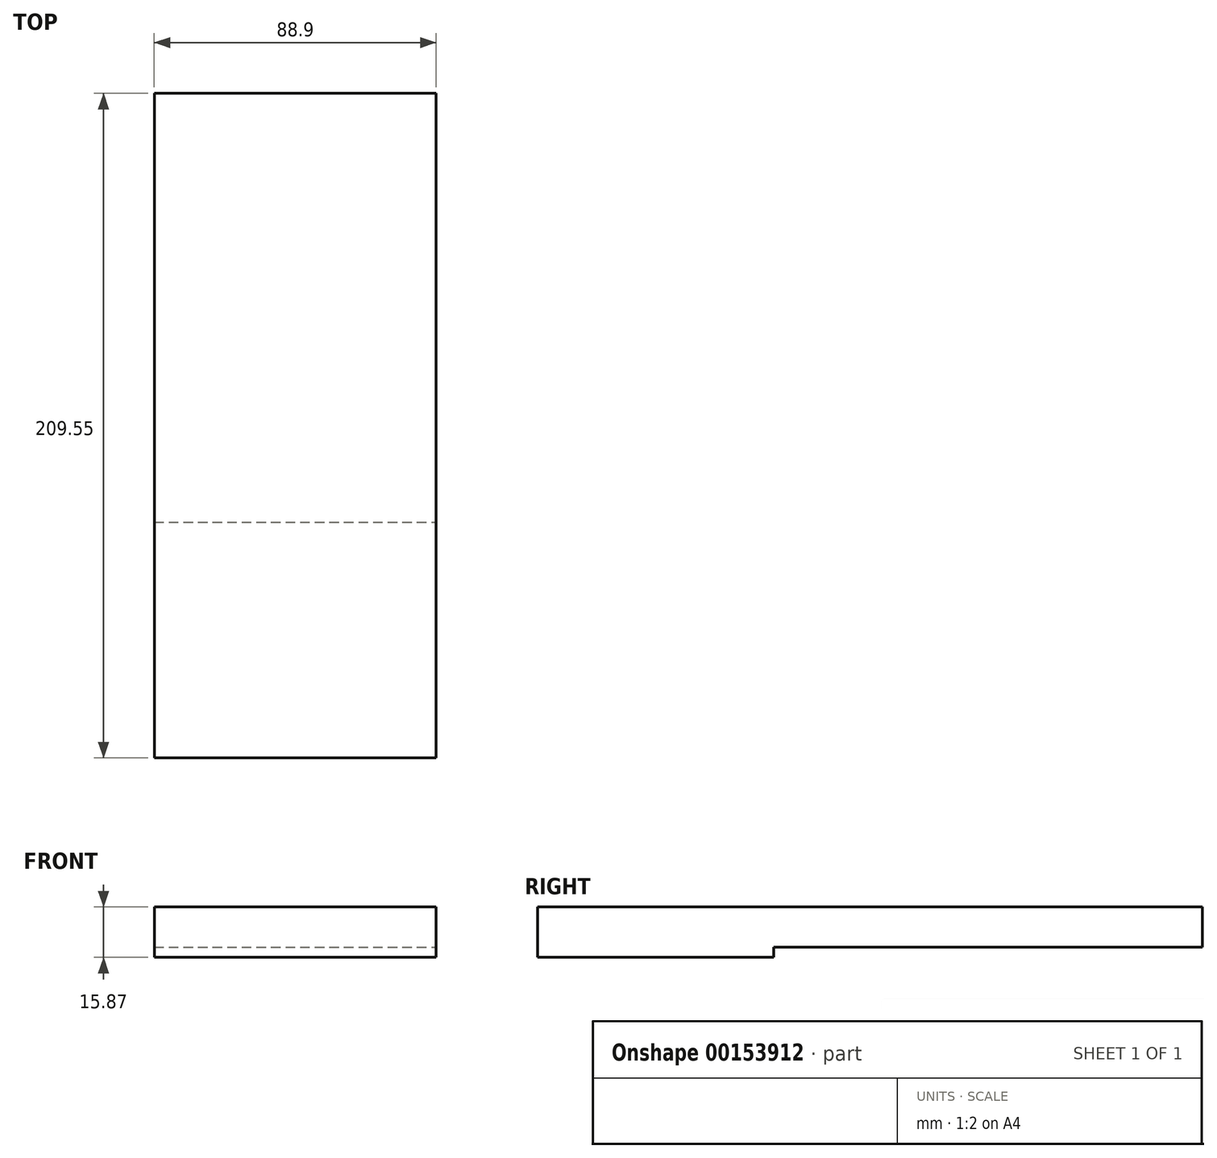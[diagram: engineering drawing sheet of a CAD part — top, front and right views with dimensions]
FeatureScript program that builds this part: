
annotation { "Feature Type Name" : "Feature", "Feature Type Description" : "" }
export const myFeature = defineFeature(function(context is Context, id is Id, definition is map)
    precondition{}
    {
        {
            var Q0;
            Q0=qCreatedBy(makeId("Front.planeOp"),FACE);
            var sketch = newSketch(context, id + "F0", { "sketchPlane" : qUnion([Q0])});
            skLineSegment(sketch, "E0.bottom", {"start": v(-33.87, 12.7) * mm, "end": v(55.03, 12.7) * mm});
            skLineSegment(sketch, "E0.top", {"start": v(-33.87, 0) * mm, "end": v(55.03, 0) * mm});
            skLineSegment(sketch, "E0.left", {"start": v(-33.87, 12.7) * mm, "end": v(-33.87, 0) * mm});
            skLineSegment(sketch, "E0.right", {"start": v(55.03, 12.7) * mm, "end": v(55.03, 0) * mm});
            skSolve(sketch);
        }
        {
            var Q0;
            Q0 = qSketchRegion(id + "F0", true);
            extrude(context, id + "F1", {"entities" : qUnion([Q0]), "depth" : 209.55 * mm});
        }
        {
            var Q0;
            Q0=makeQuery(id+"F1.opExtrude","SWEPT_FACE",FACE,{"disambiguationData":[OSD([sQuery(id+"F0.wireOp",EDGE,"E0.top")])]});
            var sketch = newSketch(context, id + "F2", { "sketchPlane" : qUnion([Q0])});
            skLineSegment(sketch, "E1.bottom", {"start": v(-33.87, 209.55) * mm, "end": v(55.03, 209.55) * mm});
            skLineSegment(sketch, "E1.top", {"start": v(-33.87, 135.2) * mm, "end": v(55.03, 135.2) * mm});
            skLineSegment(sketch, "E1.left", {"start": v(-33.87, 209.55) * mm, "end": v(-33.87, 135.2) * mm});
            skLineSegment(sketch, "E1.right", {"start": v(55.03, 209.55) * mm, "end": v(55.03, 135.2) * mm});
            skSolve(sketch);
        }
        {
            var Q0;
            Q0 = qSketchRegion(id + "F2", true);
            extrude(context, id + "F3", {"entities" : qUnion([Q0]), "operationType" : NewBodyOperationType.ADD, "depth" : 3.17 * mm});
        }
    });
